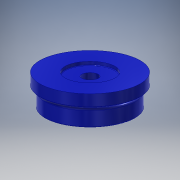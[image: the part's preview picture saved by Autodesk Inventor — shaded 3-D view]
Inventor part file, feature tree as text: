
AUTODESK INVENTOR PART (.ipt)
format: ipt  version: 2018 (Build 220112000, 112)  size: 166,400 bytes
history: native  units: mm
features: revolve x1, sketch x1
ambient origin geometry x8: Origin, YZ Plane, XZ Plane, XY Plane, X Axis, Y Axis, Z Axis, Center Point
bodies: Solid1 (feature_tree)
feature tree (2):
  revolve  "Revolution1"  [1 undecoded]
  sketch  "Sketch1"  dims[d0=10.0mm d1=12.9mm d2=8.0mm d3=20.0mm d4=18.0mm d5=1.5mm d6=3.39mm d7=13.613568mm d8=12.9mm d9=0.25mm d10=2.0mm d11=0.25mm d12=90.0deg]
note: 1 required parameter value undecoded (feature->parameter linkage not recoverable at this tier; creation-order binding heuristic only, values carry confidence <= 0.55)
